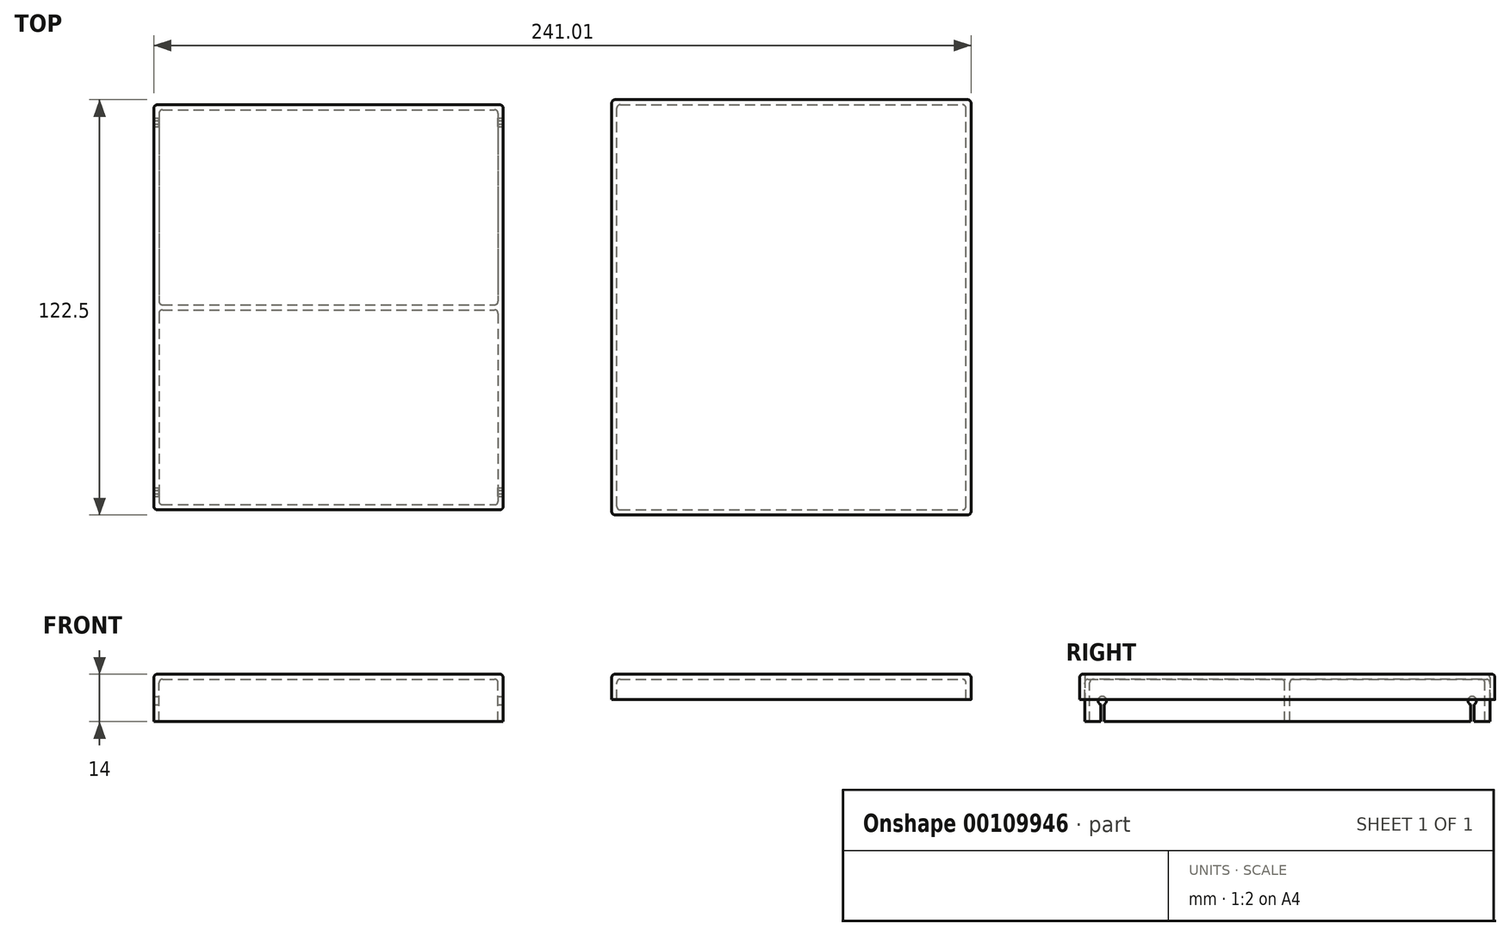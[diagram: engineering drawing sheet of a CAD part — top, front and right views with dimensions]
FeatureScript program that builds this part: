
annotation { "Feature Type Name" : "Feature", "Feature Type Description" : "" }
export const myFeature = defineFeature(function(context is Context, id is Id, definition is map)
    precondition{}
    {
        {
            var Q0;
            Q0=qCreatedBy(makeId("Top.planeOp"),FACE);
            var sketch = newSketch(context, id + "F0", { "sketchPlane" : qUnion([Q0])});
            skLineSegment(sketch, "E0.bottom", {"start": v(-89.62, 77.2) * mm, "end": v(13.38, 77.2) * mm});
            skLineSegment(sketch, "E0.top", {"start": v(-89.62, -42.3) * mm, "end": v(13.38, -42.3) * mm});
            skLineSegment(sketch, "E0.left", {"start": v(-89.62, 77.2) * mm, "end": v(-89.62, -42.3) * mm});
            skLineSegment(sketch, "E0.right", {"start": v(13.38, 77.2) * mm, "end": v(13.38, -42.3) * mm});
            skLineSegment(sketch, "E1.bottom", {"start": v(-88.12, 75.7) * mm, "end": v(11.88, 75.7) * mm});
            skLineSegment(sketch, "E1.top", {"start": v(-88.12, 18.2) * mm, "end": v(11.88, 18.2) * mm});
            skLineSegment(sketch, "E1.left", {"start": v(-88.12, 75.7) * mm, "end": v(-88.12, 18.2) * mm});
            skLineSegment(sketch, "E1.right", {"start": v(11.88, 75.7) * mm, "end": v(11.88, 18.2) * mm});
            skLineSegment(sketch, "E2.bottom", {"start": v(-88.12, 16.7) * mm, "end": v(11.88, 16.7) * mm});
            skLineSegment(sketch, "E2.top", {"start": v(-88.12, -40.8) * mm, "end": v(11.88, -40.8) * mm});
            skLineSegment(sketch, "E2.left", {"start": v(-88.12, 16.7) * mm, "end": v(-88.12, -40.8) * mm});
            skLineSegment(sketch, "E2.right", {"start": v(11.88, 16.7) * mm, "end": v(11.88, -40.8) * mm});
            skLineSegment(sketch, "E3.bottom", {"start": v(46.89, -42.3) * mm, "end": v(149.89, -42.3) * mm});
            skLineSegment(sketch, "E3.top", {"start": v(46.89, 77.2) * mm, "end": v(149.89, 77.2) * mm});
            skLineSegment(sketch, "E3.left", {"start": v(46.89, -42.3) * mm, "end": v(46.89, 77.2) * mm});
            skLineSegment(sketch, "E3.right", {"start": v(149.89, -42.3) * mm, "end": v(149.89, 77.2) * mm});
            skLineSegment(sketch, "E4.bottom", {"start": v(45.39, -43.8) * mm, "end": v(151.39, -43.8) * mm});
            skLineSegment(sketch, "E4.top", {"start": v(45.39, 78.7) * mm, "end": v(151.39, 78.7) * mm});
            skLineSegment(sketch, "E4.left", {"start": v(45.39, -43.8) * mm, "end": v(45.39, 78.7) * mm});
            skLineSegment(sketch, "E4.right", {"start": v(151.39, -43.8) * mm, "end": v(151.39, 78.7) * mm});
            skSolve(sketch);
        }
        {
            var Q0;
            Q0=makeQuery(id+"F0.imprint","IMPRINT",FACE,{"disambiguationData":[TD([[makeQuery(id+"F0.imprint","IMPRINT",EDGE,{"derivedFrom":sQuery(id+"F0.wireOp",EDGE,"E1.bottom")}),-1.0]])]});
            var Q1;
            Q1=makeQuery(id+"F0.imprint","IMPRINT",FACE,{"disambiguationData":[TD([[makeQuery(id+"F0.imprint","IMPRINT",EDGE,{"derivedFrom":sQuery(id+"F0.wireOp",EDGE,"E2.bottom")}),-1.0]])]});
            var Q2;
            Q2=makeQuery(id+"F0.imprint","IMPRINT",FACE,{"disambiguationData":[TD([[makeQuery(id+"F0.imprint","IMPRINT",EDGE,{"derivedFrom":sQuery(id+"F0.wireOp",EDGE,"E0.bottom")}),-1.0]])]});
            var Q3;
            Q3=makeQuery(id+"F0.imprint","IMPRINT",FACE,{"disambiguationData":[TD([[makeQuery(id+"F0.imprint","IMPRINT",EDGE,{"derivedFrom":sQuery(id+"F0.wireOp",EDGE,"E3.bottom")}),1.0]])]});
            var Q4;
            Q4=makeQuery(id+"F0.imprint","IMPRINT",FACE,{"disambiguationData":[TD([[makeQuery(id+"F0.imprint","IMPRINT",EDGE,{"derivedFrom":sQuery(id+"F0.wireOp",EDGE,"E3.bottom")}),-1.0]])]});
            extrude(context, id + "F1", {"entities" : qUnion([Q0, Q1, Q2, Q3, Q4]), "depth" : 1.5 * mm});
        }
        {
            var Q0;
            Q0=makeQuery(id+"F0.imprint","IMPRINT",FACE,{"disambiguationData":[TD([[makeQuery(id+"F0.imprint","IMPRINT",EDGE,{"derivedFrom":sQuery(id+"F0.wireOp",EDGE,"E0.bottom")}),-1.0]])]});
            var Q1;
            Q1=sQuery(id+"F0.wireOp",EDGE,"E1.top");
            extrude(context, id + "F2", {"entities" : qUnion([Q0]), "operationType" : NewBodyOperationType.ADD, "surfaceEntities" : qUnion([Q1]), "oppositeDirection" : true, "depth" : 12.5 * mm});
        }
        {
            var Q0;
            {var subQ0=sQuery(id+"F0.wireOp",EDGE,"E0.right");Q0=makeQuery(id+"F2.boolean.opBoolean","MERGE",FACE,{"derivedFrom":[makeQuery(id+"F1.opExtrude","SWEPT_FACE",FACE,{"disambiguationData":[OSD([subQ0])]}),makeQuery(id+"F2.opExtrude","SWEPT_FACE",FACE,{"disambiguationData":[OSD([subQ0])]})]});}
            var sketch = newSketch(context, id + "F3", { "sketchPlane" : qUnion([Q0])});
            skPoint(sketch, "E5", {"position": v(-37.1, -6.3) * mm});
            skPoint(sketch, "E6", {"position": v(72, -6.3) * mm});
            skCircle(sketch, "E7", {"center": v(-37.1, -6.3) * mm, "radius": 1.25 * mm});
            skCircle(sketch, "E8", {"center": v(72, -6.3) * mm, "radius": 1.25 * mm});
            skLineSegment(sketch, "E9.bottom", {"start": v(-37.6, -6.3) * mm, "end": v(-36.6, -6.3) * mm});
            skLineSegment(sketch, "E9.top", {"start": v(-37.6, -12.5) * mm, "end": v(-36.6, -12.5) * mm});
            skLineSegment(sketch, "E9.left", {"start": v(-37.6, -6.3) * mm, "end": v(-37.6, -12.5) * mm});
            skLineSegment(sketch, "E9.right", {"start": v(-36.6, -6.3) * mm, "end": v(-36.6, -12.5) * mm});
            skLineSegment(sketch, "E10.bottom", {"start": v(71.5, -6.3) * mm, "end": v(72.5, -6.3) * mm});
            skLineSegment(sketch, "E10.top", {"start": v(71.5, -12.5) * mm, "end": v(72.5, -12.5) * mm});
            skLineSegment(sketch, "E10.left", {"start": v(71.5, -6.3) * mm, "end": v(71.5, -12.5) * mm});
            skLineSegment(sketch, "E10.right", {"start": v(72.5, -6.3) * mm, "end": v(72.5, -12.5) * mm});
            skSolve(sketch);
        }
        {
            var Q0;
            Q0=makeQuery(id+"F0.imprint","IMPRINT",FACE,{"disambiguationData":[TD([[makeQuery(id+"F0.imprint","IMPRINT",EDGE,{"derivedFrom":sQuery(id+"F0.wireOp",EDGE,"E3.bottom")}),-1.0]])]});
            extrude(context, id + "F4", {"entities" : qUnion([Q0]), "operationType" : NewBodyOperationType.ADD, "oppositeDirection" : true, "depth" : 6 * mm});
        }
        {
            var Q0;
            {var subQ5=sQuery(id+"F3.wireOp",EDGE,"E9.bottom");Q0=makeQuery(id+"F3.imprint","IMPRINT",FACE,{"disambiguationData":[TD([[makeQuery(id+"F3.imprint","IMPRINT",EDGE,{"derivedFrom":subQ5}),1.0]])]});}
            var Q1;
            {var subQ5=sQuery(id+"F3.wireOp",EDGE,"E9.bottom");Q1=makeQuery(id+"F3.imprint","IMPRINT",FACE,{"disambiguationData":[TD([[makeQuery(id+"F3.imprint","IMPRINT",EDGE,{"derivedFrom":subQ5}),-1.0]])]});}
            var Q2;
            {var subQ5=sQuery(id+"F3.wireOp",EDGE,"E9.top");Q2=makeQuery(id+"F3.imprint","IMPRINT",FACE,{"disambiguationData":[TD([[makeQuery(id+"F3.imprint","IMPRINT",EDGE,{"derivedFrom":subQ5}),-1.0]])]});}
            var Q3;
            {var subQ5=sQuery(id+"F3.wireOp",EDGE,"E10.bottom");Q3=makeQuery(id+"F3.imprint","IMPRINT",FACE,{"disambiguationData":[TD([[makeQuery(id+"F3.imprint","IMPRINT",EDGE,{"derivedFrom":subQ5}),-1.0]])]});}
            var Q4;
            {var subQ5=sQuery(id+"F3.wireOp",EDGE,"E10.bottom");Q4=makeQuery(id+"F3.imprint","IMPRINT",FACE,{"disambiguationData":[TD([[makeQuery(id+"F3.imprint","IMPRINT",EDGE,{"derivedFrom":subQ5}),1.0]])]});}
            var Q5;
            {var subQ5=sQuery(id+"F3.wireOp",EDGE,"E10.top");Q5=makeQuery(id+"F3.imprint","IMPRINT",FACE,{"disambiguationData":[TD([[makeQuery(id+"F3.imprint","IMPRINT",EDGE,{"derivedFrom":subQ5}),-1.0]])]});}
            extrude(context, id + "F5", {"entities" : qUnion([Q0, Q1, Q2, Q3, Q4, Q5]), "operationType" : NewBodyOperationType.REMOVE, "endBound" : BoundingType.THROUGH_ALL, "oppositeDirection" : true, "depth" : 25 * mm});
        }
        {
            var Q0;
            Q0=makeQuery(id+"F1.opExtrude","CAP_EDGE",EDGE,{"disambiguationData":[OSD([sQuery(id+"F0.wireOp",EDGE,"E0.right")])],"isStart":false});
            var Q1;
            Q1=makeQuery(id+"F1.opExtrude","CAP_EDGE",EDGE,{"disambiguationData":[OSD([sQuery(id+"F0.wireOp",EDGE,"E0.bottom")])],"isStart":false});
            var Q2;
            Q2=makeQuery(id+"F1.opExtrude","CAP_EDGE",EDGE,{"disambiguationData":[OSD([sQuery(id+"F0.wireOp",EDGE,"E0.left")])],"isStart":false});
            var Q3;
            Q3=makeQuery(id+"F1.opExtrude","CAP_EDGE",EDGE,{"disambiguationData":[OSD([sQuery(id+"F0.wireOp",EDGE,"E0.top")])],"isStart":false});
            var Q4;
            {var subQ0=sQuery(id+"F0.wireOp",EDGE,"E0.right");var subQ1=sQuery(id+"F0.wireOp",EDGE,"E0.bottom");Q4=makeQuery(id+"F2.boolean.opBoolean","MERGE",EDGE,{"derivedFrom":[makeQuery(id+"F1.opExtrude","SWEPT_EDGE",EDGE,{"disambiguationData":[OSD([subQ1,subQ0])]}),makeQuery(id+"F2.opExtrude","SWEPT_EDGE",EDGE,{"disambiguationData":[OSD([subQ1,subQ0])]})]});}
            var Q5;
            {var subQ0=sQuery(id+"F0.wireOp",EDGE,"E0.left");var subQ1=sQuery(id+"F0.wireOp",EDGE,"E0.bottom");Q5=makeQuery(id+"F2.boolean.opBoolean","MERGE",EDGE,{"derivedFrom":[makeQuery(id+"F1.opExtrude","SWEPT_EDGE",EDGE,{"disambiguationData":[OSD([subQ1,subQ0])]}),makeQuery(id+"F2.opExtrude","SWEPT_EDGE",EDGE,{"disambiguationData":[OSD([subQ1,subQ0])]})]});}
            var Q6;
            {var subQ0=sQuery(id+"F0.wireOp",EDGE,"E0.right");var subQ1=sQuery(id+"F0.wireOp",EDGE,"E0.top");Q6=makeQuery(id+"F2.boolean.opBoolean","MERGE",EDGE,{"derivedFrom":[makeQuery(id+"F1.opExtrude","SWEPT_EDGE",EDGE,{"disambiguationData":[OSD([subQ1,subQ0])]}),makeQuery(id+"F2.opExtrude","SWEPT_EDGE",EDGE,{"disambiguationData":[OSD([subQ1,subQ0])]})]});}
            var Q7;
            {var subQ0=sQuery(id+"F0.wireOp",EDGE,"E0.left");var subQ1=sQuery(id+"F0.wireOp",EDGE,"E0.top");Q7=makeQuery(id+"F2.boolean.opBoolean","MERGE",EDGE,{"derivedFrom":[makeQuery(id+"F1.opExtrude","SWEPT_EDGE",EDGE,{"disambiguationData":[OSD([subQ1,subQ0])]}),makeQuery(id+"F2.opExtrude","SWEPT_EDGE",EDGE,{"disambiguationData":[OSD([subQ1,subQ0])]})]});}
            var Q8;
            Q8=makeQuery(id+"F2.boolean.opBoolean","SPLIT",FACE,{"disambiguationData":[TD([makeQuery(id+"F2.opExtrude","SWEPT_FACE",FACE,{"disambiguationData":[OSD([sQuery(id+"F0.wireOp",EDGE,"E2.bottom")])]})])],"derivedFrom":makeQuery(id+"F1.opExtrude","CAP_FACE",FACE,{"disambiguationData":[OSD([sQuery(id+"F0.wireOp",EDGE,"E0.bottom"),sQuery(id+"F0.wireOp",EDGE,"E0.top"),sQuery(id+"F0.wireOp",EDGE,"E0.left"),sQuery(id+"F0.wireOp",EDGE,"E0.right")])],"isStart":true})});
            var Q9;
            Q9=makeQuery(id+"F2.boolean.opBoolean","SPLIT",FACE,{"disambiguationData":[TD([makeQuery(id+"F2.opExtrude","SWEPT_FACE",FACE,{"disambiguationData":[OSD([sQuery(id+"F0.wireOp",EDGE,"E1.bottom")])]})])],"derivedFrom":makeQuery(id+"F1.opExtrude","CAP_FACE",FACE,{"disambiguationData":[OSD([sQuery(id+"F0.wireOp",EDGE,"E0.bottom"),sQuery(id+"F0.wireOp",EDGE,"E0.top"),sQuery(id+"F0.wireOp",EDGE,"E0.left"),sQuery(id+"F0.wireOp",EDGE,"E0.right")])],"isStart":true})});
            var Q10;
            Q10=makeQuery(id+"F2.opExtrude","SWEPT_EDGE",EDGE,{"disambiguationData":[OSD([sQuery(id+"F0.wireOp",EDGE,"E2.bottom"),sQuery(id+"F0.wireOp",EDGE,"E2.right")])]});
            var Q11;
            Q11=makeQuery(id+"F2.opExtrude","SWEPT_EDGE",EDGE,{"disambiguationData":[OSD([sQuery(id+"F0.wireOp",EDGE,"E1.top"),sQuery(id+"F0.wireOp",EDGE,"E1.right")])]});
            var Q12;
            Q12=makeQuery(id+"F2.opExtrude","SWEPT_EDGE",EDGE,{"disambiguationData":[OSD([sQuery(id+"F0.wireOp",EDGE,"E2.top"),sQuery(id+"F0.wireOp",EDGE,"E2.left")])]});
            var Q13;
            Q13=makeQuery(id+"F2.opExtrude","SWEPT_EDGE",EDGE,{"disambiguationData":[OSD([sQuery(id+"F0.wireOp",EDGE,"E1.top"),sQuery(id+"F0.wireOp",EDGE,"E1.left")])]});
            var Q14;
            Q14=makeQuery(id+"F2.opExtrude","SWEPT_EDGE",EDGE,{"disambiguationData":[OSD([sQuery(id+"F0.wireOp",EDGE,"E2.bottom"),sQuery(id+"F0.wireOp",EDGE,"E2.left")])]});
            var Q15;
            Q15=makeQuery(id+"F2.opExtrude","SWEPT_EDGE",EDGE,{"disambiguationData":[OSD([sQuery(id+"F0.wireOp",EDGE,"E1.bottom"),sQuery(id+"F0.wireOp",EDGE,"E1.left")])]});
            var Q16;
            Q16=makeQuery(id+"F2.opExtrude","SWEPT_EDGE",EDGE,{"disambiguationData":[OSD([sQuery(id+"F0.wireOp",EDGE,"E1.bottom"),sQuery(id+"F0.wireOp",EDGE,"E1.right")])]});
            var Q17;
            Q17=makeQuery(id+"F2.opExtrude","SWEPT_EDGE",EDGE,{"disambiguationData":[OSD([sQuery(id+"F0.wireOp",EDGE,"E2.top"),sQuery(id+"F0.wireOp",EDGE,"E2.right")])]});
            var Q18;
            Q18=makeQuery(id+"F1.opExtrude","CAP_FACE",FACE,{"disambiguationData":[OSD([sQuery(id+"F0.wireOp",EDGE,"E4.bottom"),sQuery(id+"F0.wireOp",EDGE,"E4.top"),sQuery(id+"F0.wireOp",EDGE,"E4.left"),sQuery(id+"F0.wireOp",EDGE,"E4.right")])],"isStart":true});
            var Q19;
            Q19=makeQuery(id+"F1.opExtrude","CAP_FACE",FACE,{"disambiguationData":[OSD([sQuery(id+"F0.wireOp",EDGE,"E4.bottom"),sQuery(id+"F0.wireOp",EDGE,"E4.top"),sQuery(id+"F0.wireOp",EDGE,"E4.left"),sQuery(id+"F0.wireOp",EDGE,"E4.right")])],"isStart":false});
            var Q20;
            {var subQ0=sQuery(id+"F0.wireOp",EDGE,"E4.right");var subQ1=sQuery(id+"F0.wireOp",EDGE,"E4.top");Q20=makeQuery(id+"F4.boolean.opBoolean","MERGE",EDGE,{"derivedFrom":[makeQuery(id+"F1.opExtrude","SWEPT_EDGE",EDGE,{"disambiguationData":[OSD([subQ1,subQ0])]}),makeQuery(id+"F4.opExtrude","SWEPT_EDGE",EDGE,{"disambiguationData":[OSD([subQ1,subQ0])]})]});}
            var Q21;
            {var subQ0=sQuery(id+"F0.wireOp",EDGE,"E4.left");var subQ1=sQuery(id+"F0.wireOp",EDGE,"E4.top");Q21=makeQuery(id+"F4.boolean.opBoolean","MERGE",EDGE,{"derivedFrom":[makeQuery(id+"F1.opExtrude","SWEPT_EDGE",EDGE,{"disambiguationData":[OSD([subQ1,subQ0])]}),makeQuery(id+"F4.opExtrude","SWEPT_EDGE",EDGE,{"disambiguationData":[OSD([subQ1,subQ0])]})]});}
            var Q22;
            {var subQ0=sQuery(id+"F0.wireOp",EDGE,"E4.right");var subQ1=sQuery(id+"F0.wireOp",EDGE,"E4.bottom");Q22=makeQuery(id+"F4.boolean.opBoolean","MERGE",EDGE,{"derivedFrom":[makeQuery(id+"F1.opExtrude","SWEPT_EDGE",EDGE,{"disambiguationData":[OSD([subQ1,subQ0])]}),makeQuery(id+"F4.opExtrude","SWEPT_EDGE",EDGE,{"disambiguationData":[OSD([subQ1,subQ0])]})]});}
            var Q23;
            {var subQ0=sQuery(id+"F0.wireOp",EDGE,"E4.left");var subQ1=sQuery(id+"F0.wireOp",EDGE,"E4.bottom");Q23=makeQuery(id+"F4.boolean.opBoolean","MERGE",EDGE,{"derivedFrom":[makeQuery(id+"F1.opExtrude","SWEPT_EDGE",EDGE,{"disambiguationData":[OSD([subQ1,subQ0])]}),makeQuery(id+"F4.opExtrude","SWEPT_EDGE",EDGE,{"disambiguationData":[OSD([subQ1,subQ0])]})]});}
            var Q24;
            Q24=makeQuery(id+"F4.opExtrude","SWEPT_EDGE",EDGE,{"disambiguationData":[OSD([sQuery(id+"F0.wireOp",EDGE,"E3.bottom"),sQuery(id+"F0.wireOp",EDGE,"E3.left")])]});
            var Q25;
            Q25=makeQuery(id+"F4.opExtrude","SWEPT_EDGE",EDGE,{"disambiguationData":[OSD([sQuery(id+"F0.wireOp",EDGE,"E3.top"),sQuery(id+"F0.wireOp",EDGE,"E3.left")])]});
            var Q26;
            Q26=makeQuery(id+"F4.opExtrude","SWEPT_EDGE",EDGE,{"disambiguationData":[OSD([sQuery(id+"F0.wireOp",EDGE,"E3.top"),sQuery(id+"F0.wireOp",EDGE,"E3.right")])]});
            var Q27;
            Q27=makeQuery(id+"F4.opExtrude","SWEPT_EDGE",EDGE,{"disambiguationData":[OSD([sQuery(id+"F0.wireOp",EDGE,"E3.bottom"),sQuery(id+"F0.wireOp",EDGE,"E3.right")])]});
            fillet(context, id + "F6", {"entities" : qUnion([Q0, Q1, Q2, Q3, Q4, Q5, Q6, Q7, Q8, Q9, Q10, Q11, Q12, Q13, Q14, Q15, Q16, Q17, Q18, Q19, Q20, Q21, Q22, Q23, Q24, Q25, Q26, Q27]), "radius" : 1 * mm, "tangentPropagation" : true, "allowEdgeOverflow" : false});
        }
    });
